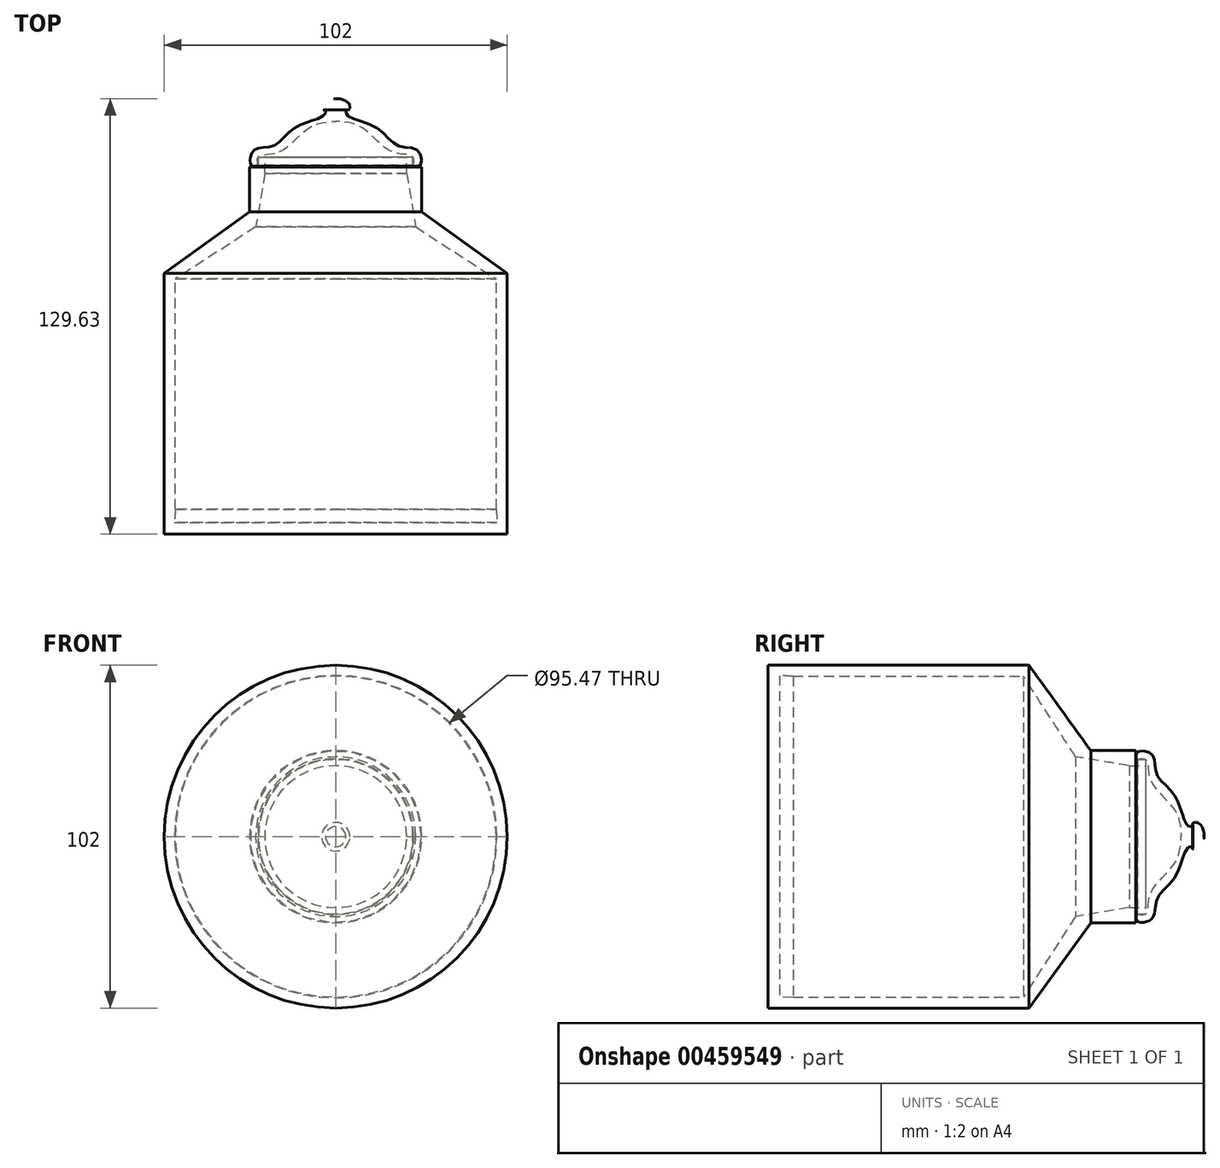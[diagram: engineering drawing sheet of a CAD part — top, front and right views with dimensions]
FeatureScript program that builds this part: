
annotation { "Feature Type Name" : "Feature", "Feature Type Description" : "" }
export const myFeature = defineFeature(function(context is Context, id is Id, definition is map)
    precondition{}
    {
        {
            var Q0;
            Q0=qCreatedBy(makeId("Top.planeOp"),FACE);
            var sketch = newSketch(context, id + "F0", { "sketchPlane" : qUnion([Q0])});
            skLineSegment(sketch, "E0", {"start": v(0, 75.43) * mm, "end": v(0, -74.6) * mm});
            skLineSegment(sketch, "E1", {"start": v(47.74, -46.7) * mm, "end": v(47.74, 21.8) * mm});
            skLineSegment(sketch, "E2", {"start": v(47.74, 21.8) * mm, "end": v(23.8, 37.28) * mm});
            skLineSegment(sketch, "E3", {"start": v(21.1, 53.25) * mm, "end": v(21.1, 58.07) * mm});
            skLineSegment(sketch, "E4", {"start": v(21.1, 58.07) * mm, "end": v(22.95, 58.07) * mm});
            skLineSegment(sketch, "E5", {"start": v(22.95, 58.07) * mm, "end": v(22.95, 55.14) * mm});
            skLineSegment(sketch, "E6", {"start": v(25.61, 41.82) * mm, "end": v(51, 23.47) * mm});
            skLineSegment(sketch, "E7", {"start": v(51, -54.15) * mm, "end": v(-12.94, -54.15) * mm});
            skFitSpline(sketch, "E8", {"points": [v(23.16, 55.66) * mm, v(22.77, 58.44) * mm, v(17.01, 59.54) * mm, v(8.37, 66.5) * mm, v(-0.37, 68.71) * mm], "startDerivative": vector(3.71, 23.82) * mm, "endDerivative": vector(-37.95, 1.07) * mm});
            skFitSpline(sketch, "E9", {"points": [v(23.16, 55.66) * mm, v(25.14, 55.66) * mm, v(24.54, 59.9) * mm, v(18.5, 61.5) * mm, v(11.86, 67.01) * mm, v(3.27, 70.74) * mm, v(3.27, 72.15) * mm, v(3.94, 72.15) * mm, v(3.94, 74.06) * mm, v(0, 75.43) * mm, v(-1.08, 74.46) * mm], "startDerivative": vector(31.64, -10.4) * mm, "endDerivative": vector(-11.41, -20) * mm});
            skLineSegment(sketch, "E10", {"start": v(-12.94, -50.7) * mm, "end": v(32.98, -50.7) * mm});
            skLineSegment(sketch, "E11", {"start": v(32.98, -50.7) * mm, "end": v(47.94, -50.7) * mm});
            skLineSegment(sketch, "E12", {"start": v(47.94, -50.7) * mm, "end": v(47.74, -46.7) * mm});
            skLineSegment(sketch, "E13", {"start": v(51, 23.47) * mm, "end": v(51, -54.15) * mm});
            skPoint(sketch, "E14.orphan", {"position": v(53.32, 21.8) * mm});
            skLineSegment(sketch, "E15", {"start": v(22.95, 55.14) * mm, "end": v(25.61, 55.14) * mm});
            skLineSegment(sketch, "E16", {"start": v(25.61, 55.14) * mm, "end": v(25.61, 41.82) * mm});
            skLineSegment(sketch, "E17", {"start": v(21.1, 53.25) * mm, "end": v(23.8, 37.28) * mm});
            skSolve(sketch);
        }
        {
            var Q0;
            {var subQ0=sQuery(id+"F0.wireOp",EDGE,"E9");var subQ1=sQuery(id+"F0.wireOp",EDGE,"E0");var subQ2=makeQuery(id+"F0.imprint","INTERSECT",VERTEX,{"derivedFrom":[subQ1,subQ0]});Q0=makeQuery(id+"F0.imprint","IMPRINT",FACE,{"disambiguationData":[TD([[makeQuery(id+"F0.imprint","IMPRINT",EDGE,{"disambiguationData":[TD([[subQ2,-1.0]])],"derivedFrom":subQ1}),1.0]])]});}
            var Q1;
            {var subQ0=sQuery(id+"F0.wireOp",EDGE,"E1");Q1=makeQuery(id+"F0.imprint","IMPRINT",FACE,{"disambiguationData":[TD([[makeQuery(id+"F0.imprint","IMPRINT",EDGE,{"derivedFrom":subQ0}),-1.0]])]});}
            var Q2;
            Q2=sQuery(id+"F0.wireOp",EDGE,"E0");
            revolve(context, id + "F1", {"entities" : qUnion([Q0, Q1]), "axis" : qUnion([Q2]), "revolveType" : RevolveType.FULL});
        }
    });
